# Revit family: 799350001_Regadera Cascade con brazo
name_source: partatom
category: Plumbing Fixtures
units: mm (PartAtom-declared; Revit-internal decimal feet)

## family parameters
Always vertical = Yes
Cut with Voids When Loaded = No
Host = Wall
OmniClass Number = 23.31.15.11
OmniClass Title = Bath Shower Units
Part Type = Normal
Room Calculation Point = No
Round Connector Dimension = Use Diameter
Shared = No

## types (1)
- Type 1
    Alto = 180 mm
    Altura ducha = 2000 mm  [stored 6.56168 ft]
    Ancho = 146 mm
    Capacidad de flujo = 80 psi: 9,5 L/min
    Creado por = IDD
    Description = La línea de griferías y accesorios plásticos Cascade se inspira en la fluidez natural
del agua y las formas creadas a su paso en caídas y cascadas, sus líneas fluidas
crean un solo viaje alrededor del producto generando formas limpias y un
acabado perfecto que resalta la precisión del diseño.
• Regadera que ayuda a ahorrar agua, consume 9,3 litros por minuto.
• Tecnologia Duracrome: acabado superior, mayor espesor en el cromado que
lo hace más brillante y resistente a la corrosión.
• Tecnología multi flow con botón selector de funciones: solo un click cambia
el tipo de chorro para una experiencia diferente en la ducha.
• Brazo articulado: permite cambiar la posición de la regadera para mayor control
de la salida del agua.
    Fabricante = Corona
    Fecha de creación = 12/08/2020
    Garantía = 30 años
    Manufacturer = Corona
    Material = Corona_Cromado
    Model = Regadera con brazo
    Peso neto = 510 g. - 1,12 lb.
    Presion maxima = 125 psi (862 Kpa)
    Presion minima = 20 psi (138 Kpa)
    Profundidad = 284 mm
    Referencia = CA4045551
    Temperatura de uso = 5˚C a 71˚C.
    Vida útil = 10.000 ciclos.

note: [stored X ft] marks values corroborated as IEEE doubles in the binary element streams (Revit-internal decimal feet)

## geometry (parser evidence)
native form markers: Sweep x8
no freeform markers — native parametric forms only
